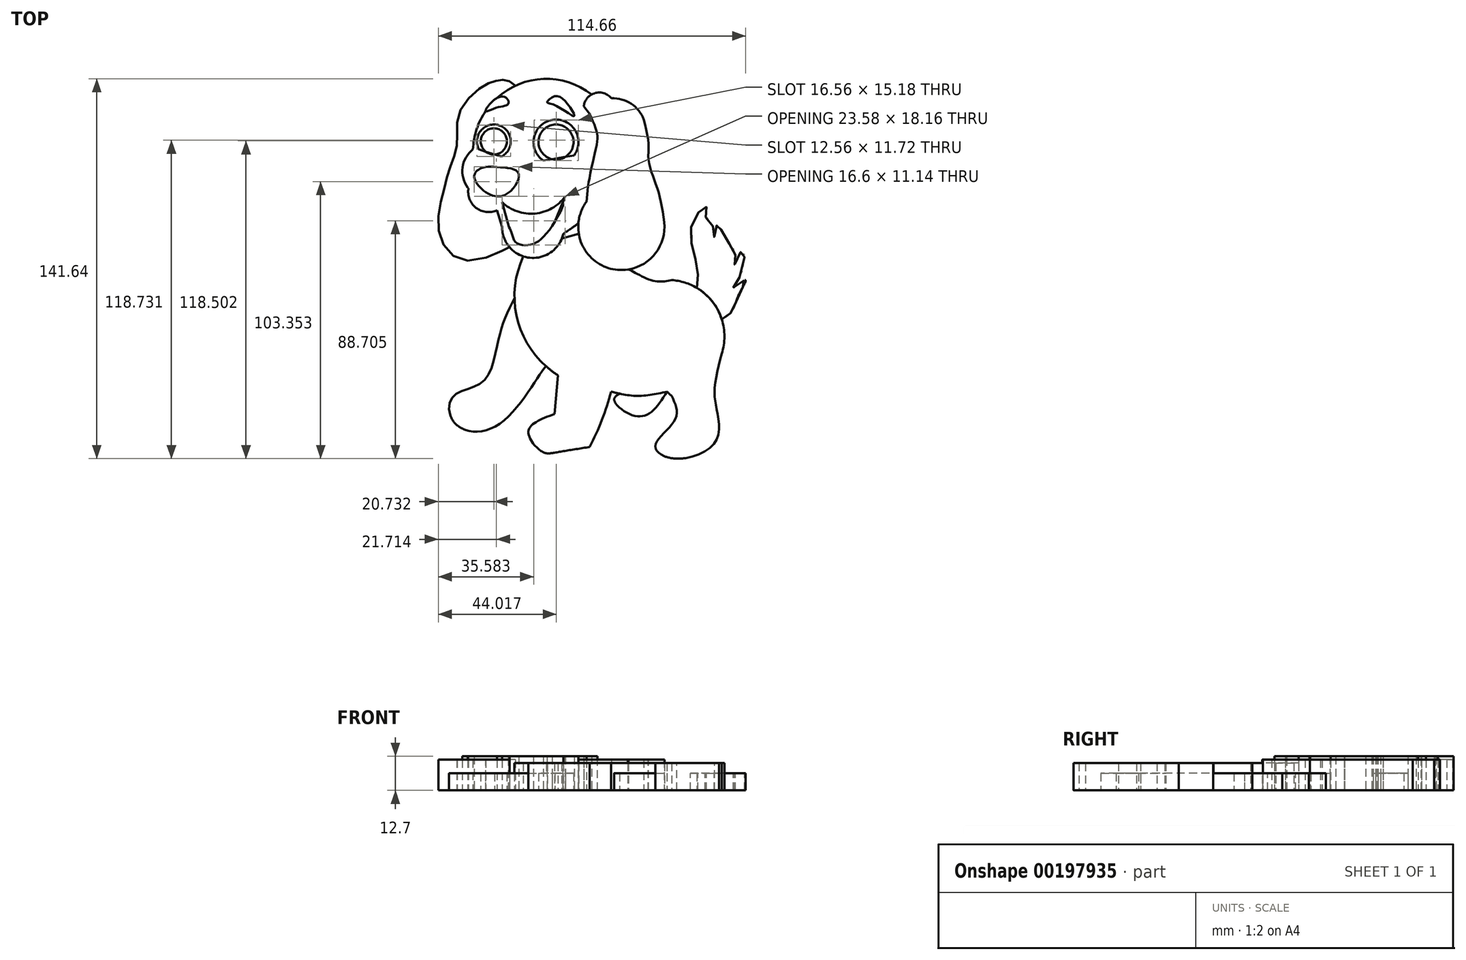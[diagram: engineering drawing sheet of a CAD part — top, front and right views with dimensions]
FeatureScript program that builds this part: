
annotation { "Feature Type Name" : "Feature", "Feature Type Description" : "" }
export const myFeature = defineFeature(function(context is Context, id is Id, definition is map)
    precondition{}
    {
        {
            var Q0;
            Q0=qCreatedBy(makeId("Top.planeOp"),FACE);
            var sketch = newSketch(context, id + "F0", { "sketchPlane" : qUnion([Q0])});
            skLineSegment(sketch, "E0", {"start": v(-13.23, -38.42) * mm, "end": v(-15.76, -67.24) * mm});
            skLineSegment(sketch, "E1", {"start": v(-21.55, 26.95) * mm, "end": v(-7, 29.48) * mm});
            skLineSegment(sketch, "E2", {"start": v(-43.99, 31.4) * mm, "end": v(-35.67, 28.73) * mm});
            skArc(sketch, "E3", {"start": v(-46.21, 31.4) * mm, "mid": v(-50.08, 24.67) * mm, "end": v(-48.15, 17.14) * mm});
            skArc(sketch, "E4", {"start": v(-1.94, 51.9) * mm, "mid": v(-30.35, 55.2) * mm, "end": v(-46.21, 31.4) * mm});
            skArc(sketch, "E5", {"start": v(6.68, 45.97) * mm, "mid": v(1.64, 52.6) * mm, "end": v(-4.91, 47.45) * mm});
            skArc(sketch, "E6", {"start": v(17.52, 42.55) * mm, "mid": v(12.75, 48.45) * mm, "end": v(5.44, 50.48) * mm});
            skArc(sketch, "E7", {"start": v(-3.87, 11.94) * mm, "mid": v(4.98, -13.03) * mm, "end": v(25.1, 4.22) * mm});
            skArc(sketch, "E8", {"start": v(-35.37, 2.43) * mm, "mid": v(-25.01, -8.99) * mm, "end": v(-12.49, 0) * mm});
            skArc(sketch, "E9", {"start": v(-37.3, 13.87) * mm, "mid": v(-23.23, 7.49) * mm, "end": v(-10.4, 16.1) * mm});
            skArc(sketch, "E10", {"start": v(-47.9, 16.97) * mm, "mid": v(-45.09, 9.65) * mm, "end": v(-37.3, 8.72) * mm});
            skArc(sketch, "E11", {"start": v(-8.47, 29.22) * mm, "mid": v(-16.67, 42.41) * mm, "end": v(-19.94, 27.23) * mm});
            skArc(sketch, "E12", {"start": v(-35.67, 28.73) * mm, "mid": v(-36.5, 40.4) * mm, "end": v(-43.99, 31.4) * mm});
            skCircle(sketch, "E13", {"center": v(-38.44, 34.4) * mm, "radius": 4.88 * mm});
            skCircle(sketch, "E14", {"center": v(-15.23, 34.16) * mm, "radius": 6.54 * mm});
            skLineSegment(sketch, "E15", {"start": v(-13.96, 17.76) * mm, "end": v(-10.4, 16.1) * mm});
            skLineSegment(sketch, "E16", {"start": v(-10.4, 16.1) * mm, "end": v(-7.84, 15.28) * mm});
            skArc(sketch, "E17", {"start": v(-27.41, -8.47) * mm, "mid": v(-29.34, -33.1) * mm, "end": v(-14.5, -52.83) * mm});
            skArc(sketch, "E18", {"start": v(-2.73, -79.53) * mm, "mid": v(5.33, -58.93) * mm, "end": v(8.65, -37.06) * mm});
            skArc(sketch, "E19", {"start": v(19.24, -41.03) * mm, "mid": v(21.25, -51.78) * mm, "end": v(27.87, -60.5) * mm});
            skArc(sketch, "E20", {"start": v(46.54, -44.78) * mm, "mid": v(43.92, -26.5) * mm, "end": v(27.87, -17.33) * mm});
            skFitSpline(sketch, "E21", {"points": [v(46.54, -44.78) * mm, v(43.9, -58.48) * mm, v(44.93, -66.81) * mm, v(44.17, -77.68) * mm, v(28.94, -83.85) * mm, v(21.78, -79.12) * mm, v(29.26, -69.12) * mm, v(27.87, -60.5) * mm], "startDerivative": vector(-23.44, -92.52) * mm, "endDerivative": vector(-32.63, 67.78) * mm});
            skFitSpline(sketch, "E22", {"points": [v(-30.73, -24.13) * mm, v(-34.43, -32.04) * mm, v(-37.28, -42.16) * mm, v(-42.83, -55.45) * mm, v(-53.43, -60.5) * mm, v(-53.45, -70.08) * mm, v(-36.73, -71.2) * mm, v(-18.9, -49.53) * mm, v(-18.42, -49.94) * mm], "startDerivative": vector(-36.24, -70.25) * mm, "endDerivative": vector(11.02, -25.67) * mm});
            skFitSpline(sketch, "E23", {"points": [v(-15.76, -67.24) * mm, v(-25.54, -73.68) * mm, v(-20.47, -81.25) * mm, v(-15.76, -81.67) * mm, v(-2.73, -79.53) * mm], "startDerivative": vector(-50.66, -18.55) * mm, "endDerivative": vector(50.1, 8.13) * mm});
            skPoint(sketch, "E24.2.internal.snap0", {"position": v(5.33, -58.93) * mm});
            skFitSpline(sketch, "E24", {"points": [v(5.33, -58.93) * mm, v(14.94, -60.5) * mm, v(26.16, -58.93) * mm], "startDerivative": vector(19.57, -4.74) * mm, "endDerivative": vector(22.04, 4.63) * mm});
            skFitSpline(sketch, "E25", {"points": [v(8.47, -59.7) * mm, v(6.43, -61.93) * mm, v(12.1, -67.24) * mm, v(19.24, -67.24) * mm, v(26.16, -58.93) * mm], "startDerivative": vector(-18.93, -11.3) * mm, "endDerivative": vector(20.58, 32.57) * mm});
            skFitSpline(sketch, "E26", {"points": [v(-45.74, 21.04) * mm, v(-42.56, 24.63) * mm, v(-36.58, 24.8) * mm, v(-29.72, 23.29) * mm, v(-29.88, 18.88) * mm, v(-37.3, 13.87) * mm, v(-45.74, 21.04) * mm]});
            skFitSpline(sketch, "E27", {"points": [v(-15.76, 51.24) * mm, v(-18.53, 49) * mm, v(-15.76, 47.97) * mm, v(-8.5, 43.83) * mm, v(-11.17, 48.73) * mm, v(-15.76, 51.24) * mm]});
            skFitSpline(sketch, "E28", {"points": [v(-2.73, 44.6) * mm, v(0, 37.92) * mm, v(0, 33.6) * mm, v(-2.73, 21.04) * mm, v(-3.87, 11.94) * mm], "startDerivative": vector(14.39, -30.73) * mm, "endDerivative": vector(-2.68, -31.34) * mm});
            skFitSpline(sketch, "E29", {"points": [v(17.52, 42.55) * mm, v(19.24, 33.54) * mm, v(19.24, 27.58) * mm, v(21.03, 21.04) * mm, v(23.41, 13.87) * mm, v(25.1, 4.22) * mm], "startDerivative": vector(10.91, -43.78) * mm, "endDerivative": vector(6.28, -44.86) * mm});
            skPoint(sketch, "E30.3.internal.snap0", {"position": v(-30.35, 55.2) * mm});
            skFitSpline(sketch, "E30", {"points": [v(-30.35, 55.2) * mm, v(-33.85, 57.27) * mm, v(-37.3, 57.1) * mm, v(-42.21, 55.2) * mm, v(-51.48, 44.68) * mm, v(-52.1, 33.67) * mm, v(-54.65, 25.17) * mm, v(-57.35, 15.19) * mm, v(-58.71, 0) * mm, v(-47.83, -10.07) * mm, v(-32.62, -4.97) * mm, v(-33.05, -5.24) * mm], "startDerivative": vector(-54.49, 41.8) * mm, "endDerivative": vector(-31.38, -19.32) * mm});
            skFitSpline(sketch, "E31", {"points": [v(-35.37, 2.43) * mm, v(-37.3, 8.72) * mm], "startDerivative": vector(-1.93, 6.3) * mm, "endDerivative": vector(-1.93, 6.3) * mm});
            skFitSpline(sketch, "E32", {"points": [v(-42.56, 24.63) * mm, v(-35.67, 28.73) * mm, v(-31.35, 28.73) * mm], "startDerivative": vector(12.45, 9.16) * mm, "endDerivative": vector(9.82, -1.5) * mm});
            skFitSpline(sketch, "E33", {"points": [v(-12.49, 0) * mm, v(-6.86, 4.1) * mm, v(-6.84, 4.3) * mm, v(-6.84, 4.33) * mm], "startDerivative": vector(9.87, 6.44) * mm, "endDerivative": vector(0.12, 0.4) * mm});
            skFitSpline(sketch, "E34", {"points": [v(-13.06, -1.84) * mm, v(-6.75, 0) * mm], "startDerivative": vector(6.32, 1.83) * mm, "endDerivative": vector(6.32, 1.83) * mm});
            skFitSpline(sketch, "E35", {"points": [v(27.87, -17.33) * mm, v(20.1, -17.33) * mm, v(11.83, -13.35) * mm, v(11.5, -13.4) * mm], "startDerivative": vector(-16.38, -3.27) * mm, "endDerivative": vector(-2.43, -1.55) * mm});
            skFitSpline(sketch, "E36", {"points": [v(37.3, -20.26) * mm, v(37.58, -13.26) * mm, v(35.2, -3.15) * mm, v(36.57, 6.08) * mm, v(40.76, 10.12) * mm, v(40.45, 6.4) * mm, v(43.43, 2.5) * mm, v(43.73, -1.18) * mm, v(45.08, 3.74) * mm, v(47.6, -1.46) * mm, v(51.63, -7.25) * mm, v(51.32, -11.57) * mm, v(54.17, -6.2) * mm, v(54, -14.53) * mm, v(51, -20.05) * mm, v(55.35, -17.33) * mm, v(52.8, -23.02) * mm, v(50.25, -29.28) * mm, v(46.56, -31.9) * mm, v(46.5, -31.73) * mm], "startDerivative": vector(15.7, 112.55) * mm, "endDerivative": vector(5.25, 25.53) * mm});
            skFitSpline(sketch, "E37", {"points": [v(-33.56, 50.42) * mm, v(-37.3, 50.57) * mm, v(-41.46, 45.78) * mm, v(-37.3, 46.98) * mm, v(-33.11, 48.34) * mm, v(-33.56, 50.42) * mm]});
            skFitSpline(sketch, "E38", {"points": [v(-36.01, 8.72) * mm, v(-34.24, 6.36) * mm, v(-32.75, 2.5) * mm, v(-31.71, 0) * mm, v(-30.22, -3.3) * mm, v(-25.14, -4.17) * mm, v(-18.83, 0) * mm, v(-12.57, 11.37) * mm, v(-13.47, 11.94) * mm], "startDerivative": vector(18.73, -20.49) * mm, "endDerivative": vector(-20.07, 3.09) * mm});
            skFitSpline(sketch, "E39", {"points": [v(-32.75, 2.5) * mm, v(-29.31, 2.5) * mm, v(-26.93, 1.33) * mm, v(-23.78, 4.53) * mm, v(-16.61, 6) * mm, v(-15.6, 4.53) * mm], "startDerivative": vector(18.66, 3.4) * mm, "endDerivative": vector(3.31, -12.58) * mm});
            skFitSpline(sketch, "E40", {"points": [v(-26.93, 1.33) * mm, v(-26.93, -1.2) * mm], "startDerivative": vector(0, -2.53) * mm, "endDerivative": vector(0, -2.53) * mm});
            skArc(sketch, "E41", {"start": v(-50.2, -61.88) * mm, "mid": v(-53.25, -64.2) * mm, "end": v(-54.68, -67.77) * mm});
            skArc(sketch, "E42", {"start": v(-44.23, -63.94) * mm, "mid": v(-47.78, -67.95) * mm, "end": v(-49.02, -73.16) * mm});
            skArc(sketch, "E43", {"start": v(-23.22, -78.88) * mm, "mid": v(-21.91, -76.13) * mm, "end": v(-20.65, -73.36) * mm});
            skArc(sketch, "E44", {"start": v(-13.93, -75.56) * mm, "mid": v(-16, -78.27) * mm, "end": v(-15.76, -81.67) * mm});
            skArc(sketch, "E45", {"start": v(27.9, -74.93) * mm, "mid": v(25.36, -78.54) * mm, "end": v(25.06, -82.95) * mm});
            skArc(sketch, "E46", {"start": v(33.11, -83.69) * mm, "mid": v(33.1, -80.49) * mm, "end": v(32.97, -77.29) * mm});
            skArc(sketch, "E47", {"start": v(10.6, -61.93) * mm, "mid": v(8.48, -61.78) * mm, "end": v(7, -63.3) * mm});
            skLineSegment(sketch, "E48", {"start": v(8.47, -59.7) * mm, "end": v(8.51, -59.67) * mm});
            skLineSegment(sketch, "E49", {"start": v(-48.15, 17.14) * mm, "end": v(-47.9, 16.97) * mm});
            skLineSegment(sketch, "E50", {"start": v(-2.73, 44.6) * mm, "end": v(-4.91, 47.45) * mm});
            skArc(sketch, "E51", {"start": v(46.56, -31.9) * mm, "mid": v(42.99, -25.24) * mm, "end": v(37.3, -20.26) * mm});
            skFitSpline(sketch, "E52", {"points": [v(-32.75, 2.5) * mm, v(-35.37, 11.7) * mm], "startDerivative": vector(-2.62, 9.21) * mm, "endDerivative": vector(-2.62, 9.21) * mm});
            skFitSpline(sketch, "E53", {"points": [v(-15.6, 4.53) * mm, v(-11.79, 13.87) * mm], "startDerivative": vector(3.82, 9.34) * mm, "endDerivative": vector(3.82, 9.34) * mm});
            skPoint(sketch, "E54.center.orphan", {"position": v(-38.44, 36.32) * mm});
            skSolve(sketch);
        }
        {
            var Q0;
            {var subQ33=sQuery(id+"F0.wireOp",EDGE,"E34");Q0=makeQuery(id+"F0.imprint","IMPRINT",FACE,{"disambiguationData":[TD([[makeQuery(id+"F0.imprint","IMPRINT",EDGE,{"derivedFrom":subQ33}),-1.0]])]});}
            extrude(context, id + "F1", {"entities" : qUnion([Q0]), "depth" : 10.16 * mm});
        }
        {
            var Q0;
            {var subQ3=sQuery(id+"F0.wireOp",EDGE,"E48");Q0=makeQuery(id+"F0.imprint","IMPRINT",FACE,{"disambiguationData":[TD([[makeQuery(id+"F0.imprint","IMPRINT",EDGE,{"derivedFrom":subQ3}),-1.0]])]});}
            var Q1;
            {var subQ0=sQuery(id+"F0.wireOp",EDGE,"E22");var subQ4=makeQuery(id+"F0.imprint","IMPRINT",VERTEX,{"disambiguationData":[OD(0.0)],"derivedFrom":subQ0});Q1=makeQuery(id+"F0.imprint","IMPRINT",FACE,{"disambiguationData":[TD([[makeQuery(id+"F0.imprint","IMPRINT",EDGE,{"disambiguationData":[TD([[subQ4,-1.0]])],"derivedFrom":subQ0}),1.0]])]});}
            extrude(context, id + "F2", {"entities" : qUnion([Q0, Q1]), "operationType" : NewBodyOperationType.ADD, "depth" : 6.35 * mm});
        }
        {
            var Q0;
            {var subQ29=sQuery(id+"F0.wireOp",EDGE,"E6");Q0=makeQuery(id+"F0.imprint","IMPRINT",FACE,{"disambiguationData":[TD([[makeQuery(id+"F0.imprint","IMPRINT",EDGE,{"derivedFrom":subQ29}),1.0]])]});}
            var Q1;
            {var subQ1=sQuery(id+"F0.wireOp",EDGE,"E3");Q1=makeQuery(id+"F0.imprint","IMPRINT",FACE,{"disambiguationData":[TD([[makeQuery(id+"F0.imprint","IMPRINT",EDGE,{"derivedFrom":subQ1}),-1.0]])]});}
            extrude(context, id + "F3", {"entities" : qUnion([Q0, Q1]), "depth" : 11.43 * mm});
        }
        {
            var Q0;
            {var subQ23=sQuery(id+"F0.wireOp",EDGE,"E3");Q0=makeQuery(id+"F0.imprint","IMPRINT",FACE,{"disambiguationData":[TD([[makeQuery(id+"F0.imprint","IMPRINT",EDGE,{"derivedFrom":subQ23}),1.0]])]});}
            extrude(context, id + "F4", {"entities" : qUnion([Q0]), "depth" : 12.7 * mm});
        }
        {
            var Q0;
            {var subQ0=sQuery(id+"F0.wireOp",EDGE,"E36");var subQ1=sQuery(id+"F0.wireOp",EDGE,"E20");var subQ2=makeQuery(id+"F0.imprint","INTERSECT",VERTEX,{"derivedFrom":[subQ1,subQ0]});Q0=makeQuery(id+"F0.imprint","IMPRINT",FACE,{"disambiguationData":[TD([[makeQuery(id+"F0.imprint","IMPRINT",EDGE,{"disambiguationData":[TD([[subQ2,1.0]])],"derivedFrom":subQ1}),-1.0]])]});}
            var Q1;
            {var subQ0=sQuery(id+"F0.wireOp",EDGE,"E38");Q1=makeQuery(id+"F0.imprint","IMPRINT",FACE,{"disambiguationData":[TD([[makeQuery(id+"F0.imprint","IMPRINT",EDGE,{"derivedFrom":subQ0}),1.0]])]});}
            var Q2;
            {var subQ0=sQuery(id+"F0.wireOp",EDGE,"E14");var subQ1=sQuery(id+"F0.wireOp",EDGE,"E1");var subQ2=makeQuery(id+"F0.imprint","INTERSECT",VERTEX,{"disambiguationData":[OD(0.0)],"derivedFrom":[subQ1,subQ0]});Q2=makeQuery(id+"F0.imprint","IMPRINT",FACE,{"disambiguationData":[TD([[makeQuery(id+"F0.imprint","IMPRINT",EDGE,{"disambiguationData":[TD([[subQ2,-1.0]])],"derivedFrom":subQ1}),1.0]])]});}
            var Q3;
            {var subQ0=sQuery(id+"F0.wireOp",EDGE,"E13");var subQ1=sQuery(id+"F0.wireOp",EDGE,"E2");var subQ2=makeQuery(id+"F0.imprint","INTERSECT",VERTEX,{"disambiguationData":[OD(0.0)],"derivedFrom":[subQ1,subQ0]});Q3=makeQuery(id+"F0.imprint","IMPRINT",FACE,{"disambiguationData":[TD([[makeQuery(id+"F0.imprint","IMPRINT",EDGE,{"disambiguationData":[TD([[subQ2,-1.0]])],"derivedFrom":subQ1}),1.0]])]});}
            extrude(context, id + "F5", {"entities" : qUnion([Q0, Q1, Q2, Q3]), "depth" : 6.35 * mm});
        }
    });
